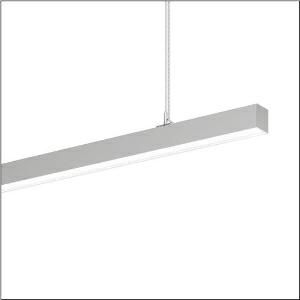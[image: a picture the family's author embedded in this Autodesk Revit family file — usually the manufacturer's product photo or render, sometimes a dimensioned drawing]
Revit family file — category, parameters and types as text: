
# Revit family: silica_r__21_51mx30dc39sb_d950
name_source: partatom
category: Lighting Fixtures
units: mm (PartAtom-declared; Revit-internal decimal feet)

## family parameters
Cut with Voids When Loaded = No
Host = Face
Light Source = No
Part Type = Normal
Room Calculation Point = No
Round Connector Dimension = Use Diameter
Shared = No

## types (1)
- --- (1 x LED, 10520 lm, 68.3 W, 3000K)
    Apparent Load = 68 VA
    CIE Flux Codes = 47 79 96 57 100
    Color Rendering = 80
    Color Temperature = 3000K
    Default Elevation = 1800 mm
    Description = Silica® 21, office luminaire, primary optical cover: cover, of PMMA, opal, light emission: direct/indirect distribution, primary light characteristic: symmetric, installation type: suspended mounting, LED, rated luminous flux: 10.520lm, luminous efficacy: 154lm/W, light colour: 830, colour temperature: 3000K, with terminal, 3+2-pole, max. 2.5mm², mains connection: 220..240V, AC, 50/60Hz, rated input power: 68.3W, luminaire housing, of aluminium, metallic grey (RAL 9006), length: 3.004mm, width: 53mm, height: 53mm, protection rating (complete): IP20, insulation class (complete): insulation class I (protective earthing), certification: CE, permissible operating ambient temperature: 0..+35°C, standard: EN 50419, packaging unit: 1 piece
    Height = 53 mm
    Lamp = 1 x LED
    Lamp Light Flux = 10520 lm
    Lamp Power = 68.3 W
    Lamp count = 1
    Length = 3004 mm
    Luminous efficacy = 154 lm/W
    Manufacturer = Siteco
    ModVariant = No
    Model = 51MX30DC39SB
    Mounting Place = Ceiling
    Mounting Type = Pendant
    Number of Poles = 1
    OnlyDefault = Yes
    Power Factor = 1
    Product Name = Silica® 21
    Product group = office luminaire | ceiling pendant
    ProductGroupID = 902
    Protection Class = Protection class I
    Protection Degree = IP 20
    RLX_Detail_Level = 1
    RLX_Emergency_Light_Flux = 0 lm
    RLX_Emergency_Type = 0
    RLX_Emergency_Type_DB = No
    RlxData = <blob elided: 23397 chars, md5=58775d9a>
    Socket = socket
    Standby Power = 0 W
    System Light Flux = 10520 lm
    System Power = 68 W
    Type Comments = factory setting: luminous flux: 100 % | dim-lin: 254 | 233 mA
    Type Image = l_1297747.jpg
    URL = http://relux.com
    VarID = @adj_047101
    Voltage = 0 V
    Weight = 0.00 kg
    Width = 53 mm

## geometry (parser evidence)
native form markers: Blend x4, Sweep x12
no freeform markers — native parametric forms only
